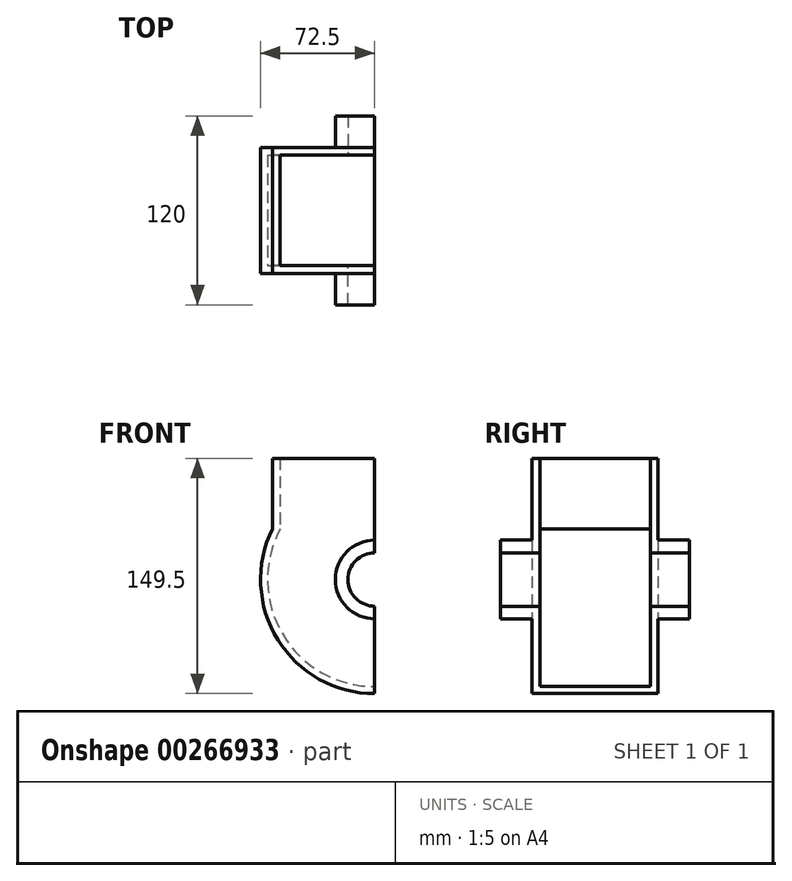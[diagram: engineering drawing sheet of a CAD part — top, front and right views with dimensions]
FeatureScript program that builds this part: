
annotation { "Feature Type Name" : "Feature", "Feature Type Description" : "" }
export const myFeature = defineFeature(function(context is Context, id is Id, definition is map)
    precondition{}
    {
        {
            var Q0;
            Q0=qCreatedBy(makeId("Front.planeOp"),FACE);
            var sketch = newSketch(context, id + "F0", { "sketchPlane" : qUnion([Q0])});
            skArc(sketch, "E0", {"start": v(0, 17) * mm, "mid": v(-17, 0) * mm, "end": v(0, -17) * mm});
            skArc(sketch, "E1", {"start": v(0, 25) * mm, "mid": v(-25, 0) * mm, "end": v(0, -25) * mm});
            skLineSegment(sketch, "E2", {"start": v(0, 25) * mm, "end": v(0, 17) * mm});
            skPoint(sketch, "E3.orphan", {"position": v(0, 39.68) * mm});
            skLineSegment(sketch, "E4.trimOffspring", {"start": v(0, -17) * mm, "end": v(0, -25) * mm});
            skSolve(sketch);
        }
        {
            var Q0;
            Q0=makeQuery(id+"F0.imprint","IMPRINT",FACE,{"disambiguationData":[TD([[makeQuery(id+"F0.imprint","IMPRINT",EDGE,{"derivedFrom":sQuery(id+"F0.wireOp",EDGE,"E0")}),-1.0]])]});
            extrude(context, id + "F1", {"entities" : qUnion([Q0]), "depth" : 20 * mm});
        }
        {
            var Q0;
            Q0=qCreatedBy(makeId("Front.planeOp"),FACE);
            var sketch = newSketch(context, id + "F2", { "sketchPlane" : qUnion([Q0])});
            skArc(sketch, "E5", {"start": v(0, 72.5) * mm, "mid": v(-72.5, 0) * mm, "end": v(0, -72.5) * mm});
            skLineSegment(sketch, "E6.0.0", {"start": v(0, 17) * mm, "end": v(0, 25) * mm});
            skArc(sketch, "E6.0.1", {"start": v(0, 25) * mm, "mid": v(-25, 0) * mm, "end": v(0, -25) * mm});
            skLineSegment(sketch, "E6.0.2", {"start": v(0, -25) * mm, "end": v(0, -17) * mm});
            skArc(sketch, "E6.0.3", {"start": v(0, -17) * mm, "mid": v(-17, 0) * mm, "end": v(0, 17) * mm});
            skLineSegment(sketch, "E7", {"start": v(0, -72.5) * mm, "end": v(0, -17) * mm});
            skLineSegment(sketch, "E8", {"start": v(0, 17) * mm, "end": v(0, 77) * mm});
            skLineSegment(sketch, "E9", {"start": v(0, 77) * mm, "end": v(-65, 77) * mm});
            skLineSegment(sketch, "E10", {"start": v(-65, 77) * mm, "end": v(-65, 32.11) * mm});
            skSolve(sketch);
        }
        {
            var Q0;
            Q0 = qSketchRegion(id + "F2", true);
            extrude(context, id + "F3", {"entities" : qUnion([Q0]), "operationType" : NewBodyOperationType.ADD, "oppositeDirection" : true, "depth" : 5 * mm});
        }
        {
            var Q0;
            Q0=qCreatedBy(makeId("Front.planeOp"),FACE);
            cPlane(context, id + "F4", {"entities" : qUnion([Q0]), "cplaneType" : CPlaneType.OFFSET, "offset" : 40 * mm, "oppositeDirection" : true, "width" : 150 * mm, "height" : 150 * mm});
        }
        {
            var Q0;
            Q0=makeQuery(id+"F1.opExtrude","SWEPT_BODY",BODY,{"disambiguationData":[OSD([sQuery(id+"F0.wireOp",EDGE,"E0"),sQuery(id+"F0.wireOp",EDGE,"E1"),sQuery(id+"F0.wireOp",EDGE,"E2"),sQuery(id+"F0.wireOp",EDGE,"E4.trimOffspring")])]});
            var Q1;
            Q1=qCreatedBy(id+"F4.planeOp",FACE);
            mirror(context, id + "F5", {"entities" : qUnion([Q0]), "mirrorPlane" : qUnion([Q1])});
        }
        {
            var Q0;
            Q0=makeQuery(id+"F3.opExtrude","CAP_FACE",FACE,{"disambiguationData":[OSD([sQuery(id+"F2.wireOp",EDGE,"E5"),sQuery(id+"F2.wireOp",EDGE,"E6.0.3"),sQuery(id+"F2.wireOp",EDGE,"E7"),sQuery(id+"F2.wireOp",EDGE,"E8"),sQuery(id+"F2.wireOp",EDGE,"E9"),sQuery(id+"F2.wireOp",EDGE,"E10")])],"isStart":false});
            var sketch = newSketch(context, id + "F6", { "sketchPlane" : qUnion([Q0])});
            skLineSegment(sketch, "E11.0", {"start": v(65, 77) * mm, "end": v(65, 32.11) * mm});
            skArc(sketch, "E12.0", {"start": v(65, 32.11) * mm, "mid": v(61.58, -38.26) * mm, "end": v(0, -72.5) * mm});
            skLineSegment(sketch, "E13", {"start": v(65, 77) * mm, "end": v(60, 77) * mm});
            skLineSegment(sketch, "E14", {"start": v(60, 77) * mm, "end": v(60, 32.11) * mm});
            skArc(sketch, "E15", {"start": v(0, -68.05) * mm, "mid": v(58.38, -34.97) * mm, "end": v(60, 32.11) * mm});
            skLineSegment(sketch, "E16", {"start": v(0, -72.5) * mm, "end": v(0, -68.05) * mm});
            skSolve(sketch);
        }
        {
            var Q0;
            Q0=makeQuery(id+"F6.imprint","IMPRINT",FACE,{"disambiguationData":[TD([[makeQuery(id+"F6.imprint","IMPRINT",EDGE,{"derivedFrom":sQuery(id+"F6.wireOp",EDGE,"E11.0")}),-1.0]])]});
            var Q1;
            Q1=makeQuery(id+"F5.opPattern","COPY",FACE,{"derivedFrom":makeQuery(id+"F3.opExtrude","CAP_FACE",FACE,{"disambiguationData":[OSD([sQuery(id+"F2.wireOp",EDGE,"E5"),sQuery(id+"F2.wireOp",EDGE,"E6.0.3"),sQuery(id+"F2.wireOp",EDGE,"E7"),sQuery(id+"F2.wireOp",EDGE,"E8"),sQuery(id+"F2.wireOp",EDGE,"E9"),sQuery(id+"F2.wireOp",EDGE,"E10")])],"isStart":false}),"instanceName":"1"});
            extrude(context, id + "F7", {"entities" : qUnion([Q0]), "operationType" : NewBodyOperationType.ADD, "endBound" : BoundingType.UP_TO_SURFACE, "endBoundEntityFace" : qUnion([Q1]), "depth" : 25 * mm});
        }
    });
